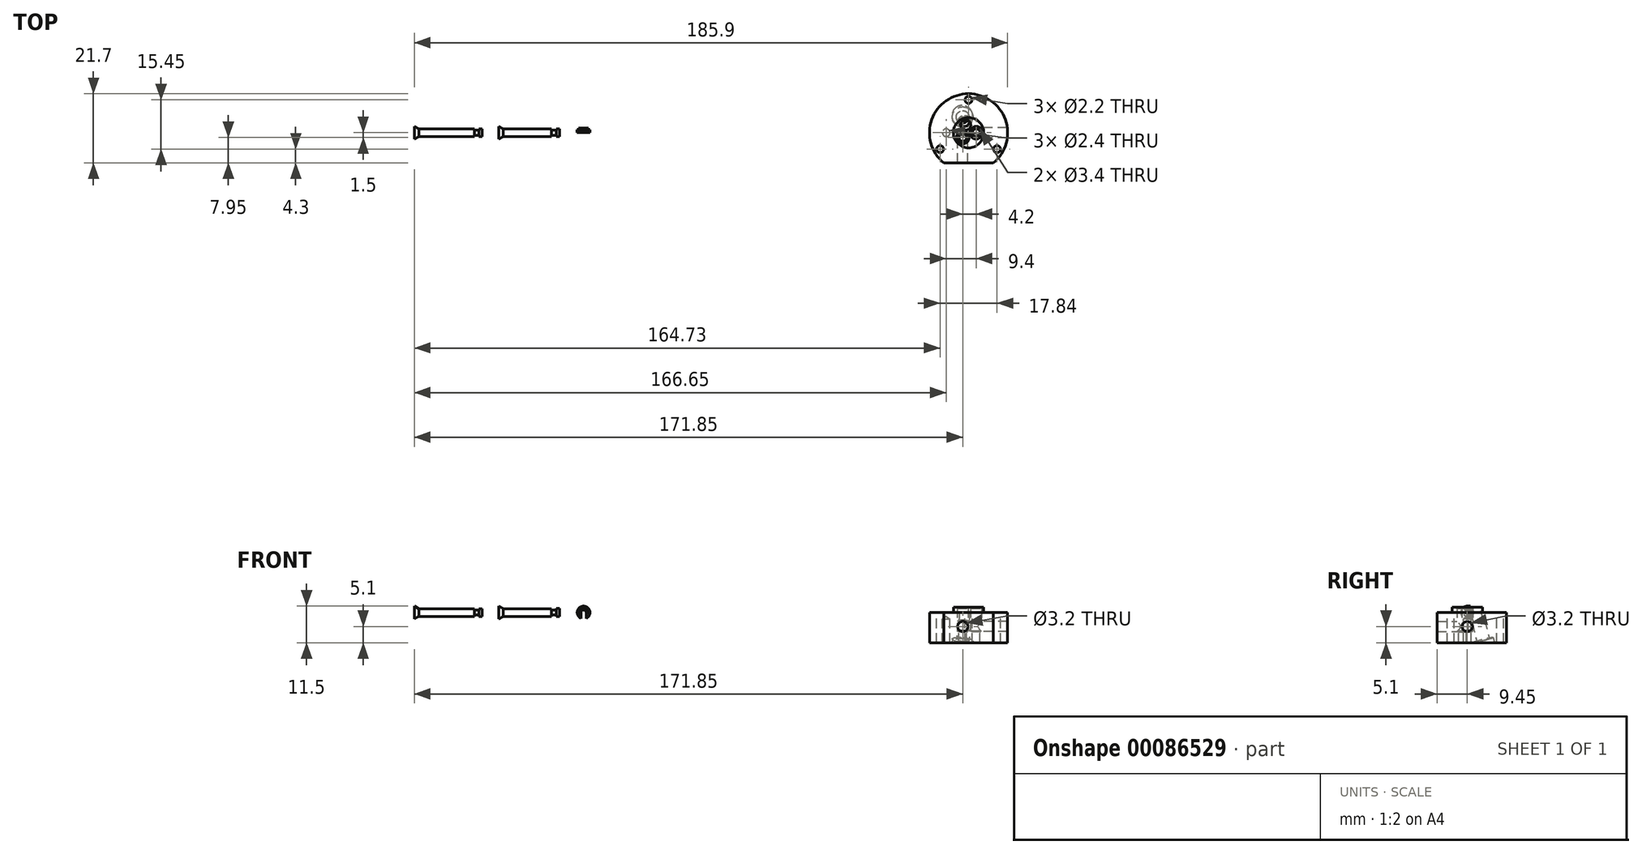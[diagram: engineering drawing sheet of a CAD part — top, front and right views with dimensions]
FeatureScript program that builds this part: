
annotation { "Feature Type Name" : "Feature", "Feature Type Description" : "" }
export const myFeature = defineFeature(function(context is Context, id is Id, definition is map)
    precondition{}
    {
        {
            var Q0;
            Q0=qCreatedBy(makeId("Top.planeOp"),FACE);
            var sketch = newSketch(context, id + "F0", { "sketchPlane" : qUnion([Q0])});
            skLineSegment(sketch, "E0", {"start": v(-7.8, -9.45) * mm, "end": v(7.8, -9.45) * mm});
            skPoint(sketch, "E1", {"position": v(0, 12.25) * mm});
            skArc(sketch, "E2", {"start": v(7.8, -9.45) * mm, "mid": v(0, 12.25) * mm, "end": v(-7.8, -9.45) * mm});
            skCircle(sketch, "E3", {"center": v(0, 0) * mm, "radius": 4.75 * mm});
            skCircle(sketch, "E4", {"center": v(0, 0) * mm, "radius": 10.3 * mm, "construction": true});
            skCircle(sketch, "E5", {"center": v(0, 10.3) * mm, "radius": 1.1 * mm});
            skCircle(sketch, "E6.1.0", {"center": v(-8.92, -5.15) * mm, "radius": 1.1 * mm});
            skCircle(sketch, "E6.2.0", {"center": v(8.92, -5.15) * mm, "radius": 1.1 * mm});
            skPoint(sketch, "E7", {"position": v(2.4, 0) * mm});
            skPoint(sketch, "E8", {"position": v(-1.8, -1.5) * mm});
            skSolve(sketch);
        }
        {
            var Q0;
            Q0=makeQuery(id+"F0.imprint","IMPRINT",FACE,{"disambiguationData":[TD([[makeQuery(id+"F0.imprint","IMPRINT",EDGE,{"derivedFrom":sQuery(id+"F0.wireOp",EDGE,"E0")}),1.0]])]});
            var Q1;
            Q1=makeQuery(id+"F0.imprint","IMPRINT",FACE,{"disambiguationData":[TD([[makeQuery(id+"F0.imprint","IMPRINT",EDGE,{"derivedFrom":sQuery(id+"F0.wireOp",EDGE,"E3")}),1.0]])]});
            extrude(context, id + "F1", {"entities" : qUnion([Q0, Q1]), "oppositeDirection" : true, "depth" : 9.5 * mm});
        }
        {
            var Q0;
            Q0=makeQuery(id+"F0.imprint","IMPRINT",FACE,{"disambiguationData":[TD([[makeQuery(id+"F0.imprint","IMPRINT",EDGE,{"derivedFrom":sQuery(id+"F0.wireOp",EDGE,"E3")}),1.0]])]});
            extrude(context, id + "F2", {"entities" : qUnion([Q0]), "operationType" : NewBodyOperationType.ADD, "depth" : 1.6 * mm});
        }
        {
            var Q0;
            Q0=makeQuery(id+"F2.opExtrude","CAP_FACE",FACE,{"disambiguationData":[OSD([sQuery(id+"F0.wireOp",EDGE,"E3"),sQuery(id+"F0.wireOp",EDGE,"RqqYGp9O-cIjH-IyXc-yckS-H4xSrRzo904b"),sQuery(id+"F0.wireOp",EDGE,"ZuBGWJ4k-Wu2v-yg4J-xYeN-5ZjtPgcVGRH9")])],"isStart":false});
            var sketch = newSketch(context, id + "F3", { "sketchPlane" : qUnion([Q0])});
            skPoint(sketch, "E9", {"position": v(-0.9, 2.4) * mm});
            skLineSegment(sketch, "E10", {"start": v(-0.9, 2.4) * mm, "end": v(-6.68, 0.23) * mm, "construction": true});
            skLineSegment(sketch, "E11.0", {"start": v(-0.34, 0.9) * mm, "end": v(-6.11, -1.26) * mm, "construction": true});
            skSolve(sketch);
        }
        {
            var Q0;
            Q0=qCreatedBy(makeId("Right.planeOp"),FACE);
            var Q1;
            Q1=sQuery(id+"F3.wireOp",EDGE,"E11.0");
            cPlane(context, id + "F4", {"entities" : qUnion([Q0, Q1]), "cplaneType" : CPlaneType.LINE_ANGLE, "offset" : 150 * mm, "angle" : 75 * degree, "width" : 150 * mm, "height" : 150 * mm});
        }
        {
            var Q0;
            Q0=qCreatedBy(id+"F4.planeOp",FACE);
            var sketch = newSketch(context, id + "F5", { "sketchPlane" : qUnion([Q0])});
            skCircle(sketch, "E12", {"center": v(-0.98, -2.72) * mm, "radius": 1.6 * mm});
            skSolve(sketch);
        }
        {
            var Q0;
            Q0=makeQuery(id+"F5.imprint","IMPRINT",FACE,{"disambiguationData":[TD([[makeQuery(id+"F5.imprint","IMPRINT",EDGE,{"derivedFrom":sQuery(id+"F5.wireOp",EDGE,"E12")}),1.0]])]});
            var Q1;
            Q1=qSketchRegion(id+"F3",true);
            extrude(context, id + "F6", {"entities" : qUnion([Q0, Q1]), "operationType" : NewBodyOperationType.REMOVE, "endBound" : BoundingType.THROUGH_ALL, "depth" : 25 * mm});
        }
        {
            var Q0;
            Q0=qCreatedBy(id+"F4.planeOp",FACE);
            cPlane(context, id + "F7", {"entities" : qUnion([Q0]), "cplaneType" : CPlaneType.OFFSET, "offset" : 15 * mm, "width" : 150 * mm, "height" : 150 * mm});
        }
        {
            var Q0;
            Q0=qCreatedBy(id+"F7.planeOp",FACE);
            var sketch = newSketch(context, id + "F8", { "sketchPlane" : qUnion([Q0])});
            skPoint(sketch, "E13.0", {"position": v(-0.98, -2.72) * mm});
            skCircle(sketch, "E14", {"center": v(-0.98, -2.72) * mm, "radius": 2 * mm});
            skSolve(sketch);
        }
        {
            var Q0;
            Q0=makeQuery(id+"F8.imprint","IMPRINT",FACE,{"disambiguationData":[TD([[makeQuery(id+"F8.imprint","IMPRINT",EDGE,{"derivedFrom":sQuery(id+"F8.wireOp",EDGE,"E14")}),1.0]])]});
            var Q1;
            Q1=sQuery(id+"F8.wireOp",EDGE,"E14");
            var Q2;
            Q2=makeQuery(id+"F1.opExtrude","CAP_FACE",FACE,{"disambiguationData":[OSD([sQuery(id+"F0.wireOp",EDGE,"E0"),sQuery(id+"F0.wireOp",EDGE,"E2"),sQuery(id+"F0.wireOp",EDGE,"E5"),sQuery(id+"F0.wireOp",EDGE,"E6.1.0"),sQuery(id+"F0.wireOp",EDGE,"E6.2.0"),sQuery(id+"F0.wireOp",EDGE,"RqqYGp9O-cIjH-IyXc-yckS-H4xSrRzo904b"),sQuery(id+"F0.wireOp",EDGE,"ZuBGWJ4k-Wu2v-yg4J-xYeN-5ZjtPgcVGRH9")])],"isStart":false});
            var Q3;
            Q3=makeQuery(id+"F1.opExtrude","SWEPT_BODY",BODY,{"disambiguationData":[OSD([sQuery(id+"F0.wireOp",EDGE,"E0"),sQuery(id+"F0.wireOp",EDGE,"E2"),sQuery(id+"F0.wireOp",EDGE,"E5"),sQuery(id+"F0.wireOp",EDGE,"E6.1.0"),sQuery(id+"F0.wireOp",EDGE,"E6.2.0"),sQuery(id+"F0.wireOp",EDGE,"RqqYGp9O-cIjH-IyXc-yckS-H4xSrRzo904b"),sQuery(id+"F0.wireOp",EDGE,"ZuBGWJ4k-Wu2v-yg4J-xYeN-5ZjtPgcVGRH9")])]});
            extrude(context, id + "F9", {"entities" : qUnion([Q0]), "operationType" : NewBodyOperationType.REMOVE, "surfaceEntities" : qUnion([Q1]), "oppositeDirection" : true, "endBoundEntityFace" : qUnion([Q2]), "endBoundEntityBody" : qUnion([Q3]), "depth" : 10 * mm});
        }
        {
            var Q0;
            Q0=qCreatedBy(id+"F7.planeOp",FACE);
            var sketch = newSketch(context, id + "F10", { "sketchPlane" : qUnion([Q0])});
            skCircle(sketch, "E15", {"center": v(-0.98, -2.72) * mm, "radius": 3.25 * mm});
            skSolve(sketch);
        }
        {
            var Q0;
            Q0=makeQuery(id+"F10.imprint","IMPRINT",FACE,{"disambiguationData":[TD([[makeQuery(id+"F10.imprint","IMPRINT",EDGE,{"derivedFrom":sQuery(id+"F10.wireOp",EDGE,"E15")}),1.0]])]});
            var Q1;
            Q1=sQuery(id+"F10.wireOp",EDGE,"E15");
            var Q2;
            Q2=makeQuery(id+"F1.opExtrude","CAP_FACE",FACE,{"disambiguationData":[OSD([sQuery(id+"F0.wireOp",EDGE,"E0"),sQuery(id+"F0.wireOp",EDGE,"E2"),sQuery(id+"F0.wireOp",EDGE,"E5"),sQuery(id+"F0.wireOp",EDGE,"E6.1.0"),sQuery(id+"F0.wireOp",EDGE,"E6.2.0"),sQuery(id+"F0.wireOp",EDGE,"RqqYGp9O-cIjH-IyXc-yckS-H4xSrRzo904b"),sQuery(id+"F0.wireOp",EDGE,"ZuBGWJ4k-Wu2v-yg4J-xYeN-5ZjtPgcVGRH9")])],"isStart":false});
            extrude(context, id + "F11", {"entities" : qUnion([Q0]), "operationType" : NewBodyOperationType.REMOVE, "surfaceEntities" : qUnion([Q1]), "oppositeDirection" : true, "endBoundEntityFace" : qUnion([Q2]), "depth" : 4 * mm});
        }
        {
            var Q0;
            Q0=makeQuery(id+"F3.imprint","IMPRINT",FACE,{"disambiguationData":[TD([[makeQuery(id+"F3.imprint","IMPRINT",EDGE,{"derivedFrom":makeQuery(id+"F2.opExtrude","CAP_EDGE",EDGE,{"disambiguationData":[OSD([sQuery(id+"F0.wireOp",EDGE,"E3")])],"isStart":false})}),1.0]])]});
            var sketch = newSketch(context, id + "F12", { "sketchPlane" : qUnion([Q0])});
            skLineSegment(sketch, "E16.0", {"start": v(-7.8, -9.45) * mm, "end": v(7.8, -9.45) * mm});
            skPoint(sketch, "E16.1", {"position": v(0, 12.25) * mm});
            skArc(sketch, "E16.2", {"start": v(7.8, -9.45) * mm, "mid": v(0, 12.25) * mm, "end": v(-7.8, -9.45) * mm});
            skCircle(sketch, "E16.3", {"center": v(0, 0) * mm, "radius": 4.75 * mm});
            skCircle(sketch, "E16.4", {"center": v(0, 0) * mm, "radius": 10.3 * mm});
            skCircle(sketch, "E16.5", {"center": v(0, 10.3) * mm, "radius": 1.1 * mm});
            skCircle(sketch, "E16.6", {"center": v(-8.92, -5.15) * mm, "radius": 1.1 * mm});
            skCircle(sketch, "E16.7", {"center": v(8.92, -5.15) * mm, "radius": 1.1 * mm});
            skPoint(sketch, "E16.8", {"position": v(0, 0) * mm});
            skPoint(sketch, "E16.9", {"position": v(2.4, 0) * mm});
            skPoint(sketch, "E16.10", {"position": v(-1.8, -1.5) * mm});
            skSolve(sketch);
        }
        {
            var Q0;
            Q0=sQuery(id+"F12.wireOp",VERTEX,"E16.10");
            var Q1;
            Q1=sQuery(id+"F12.wireOp",VERTEX,"E16.9");
            var Q2;
            Q2=makeQuery(id+"F1.opExtrude","SWEPT_BODY",BODY,{"disambiguationData":[OSD([sQuery(id+"F0.wireOp",EDGE,"E0"),sQuery(id+"F0.wireOp",EDGE,"E2"),sQuery(id+"F0.wireOp",EDGE,"E5"),sQuery(id+"F0.wireOp",EDGE,"E6.1.0"),sQuery(id+"F0.wireOp",EDGE,"E6.2.0")])]});
            hole(context, id + "F13", {"style" : HoleStyle.C_SINK, "endStyle" : HoleEndStyle.BLIND, "holeDiameter" : 3.4 * mm, "cSinkDiameter" : 4 * mm, "cSinkAngle" : 90 * degree, "holeDepth" : 7.4 * mm, "startFromSketch" : true, "locations" : qUnion([Q0, Q1]), "scope" : qUnion([Q2])});
        }
        {
            var Q0;
            Q0=makeQuery(id+"F1.opExtrude","CAP_FACE",FACE,{"disambiguationData":[OSD([sQuery(id+"F0.wireOp",EDGE,"E0"),sQuery(id+"F0.wireOp",EDGE,"E2"),sQuery(id+"F0.wireOp",EDGE,"E5"),sQuery(id+"F0.wireOp",EDGE,"E6.1.0"),sQuery(id+"F0.wireOp",EDGE,"E6.2.0")])],"isStart":false});
            var sketch = newSketch(context, id + "F14", { "sketchPlane" : qUnion([Q0])});
            skPoint(sketch, "E17.0", {"position": v(2.4, 0) * mm});
            skPoint(sketch, "E18.0", {"position": v(-1.8, 1.5) * mm});
            skSolve(sketch);
        }
        {
            var Q0;
            Q0=sQuery(id+"F14.wireOp",VERTEX,"E17.0");
            var Q1;
            Q1=sQuery(id+"F14.wireOp",VERTEX,"E18.0");
            var Q2;
            Q2=makeQuery(id+"F1.opExtrude","SWEPT_BODY",BODY,{"disambiguationData":[OSD([sQuery(id+"F0.wireOp",EDGE,"E0"),sQuery(id+"F0.wireOp",EDGE,"E2"),sQuery(id+"F0.wireOp",EDGE,"E5"),sQuery(id+"F0.wireOp",EDGE,"E6.1.0"),sQuery(id+"F0.wireOp",EDGE,"E6.2.0")])]});
            hole(context, id + "F15", {"style" : HoleStyle.SIMPLE, "endStyle" : HoleEndStyle.THROUGH, "holeDiameter" : 2.4 * mm, "startFromSketch" : true, "locations" : qUnion([Q0, Q1]), "scope" : qUnion([Q2]), "isTappedThrough" : true});
        }
        {
            var Q0;
            Q0=makeQuery(id+"F1.opExtrude","SWEPT_FACE",FACE,{"disambiguationData":[OSD([sQuery(id+"F0.wireOp",EDGE,"E0")])]});
            var sketch = newSketch(context, id + "F16", { "sketchPlane" : qUnion([Q0])});
            skLineSegment(sketch, "E19.0", {"start": v(-3.5, 1.3) * mm, "end": v(-0.1, 1.3) * mm});
            skLineSegment(sketch, "E20", {"start": v(-1.8, 1.3) * mm, "end": v(-1.8, -9.5) * mm, "construction": true});
            skLineSegment(sketch, "E21", {"start": v(-1.8, 1.3) * mm, "end": v(-3.5, 1.3) * mm});
            skLineSegment(sketch, "E22", {"start": v(-1.8, 1.3) * mm, "end": v(-0.1, 1.3) * mm});
            skPoint(sketch, "E23", {"position": v(-1.8, -4.4) * mm});
            skSolve(sketch);
        }
        {
            var Q0;
            Q0=sQuery(id+"F16.wireOp",VERTEX,"E23");
            var Q1;
            Q1=makeQuery(id+"F1.opExtrude","SWEPT_BODY",BODY,{"disambiguationData":[OSD([sQuery(id+"F0.wireOp",EDGE,"E0"),sQuery(id+"F0.wireOp",EDGE,"E2"),sQuery(id+"F0.wireOp",EDGE,"E5"),sQuery(id+"F0.wireOp",EDGE,"E6.1.0"),sQuery(id+"F0.wireOp",EDGE,"E6.2.0")])]});
            hole(context, id + "F17", {"style" : HoleStyle.SIMPLE, "endStyle" : HoleEndStyle.BLIND, "holeDiameter" : 3.2 * mm, "holeDepth" : 7.5 * mm, "startFromSketch" : true, "locations" : qUnion([Q0]), "scope" : qUnion([Q1])});
        }
        {
            var Q0;
            Q0=makeQuery(id+"F1.opExtrude","CAP_FACE",FACE,{"disambiguationData":[OSD([sQuery(id+"F0.wireOp",EDGE,"E0"),sQuery(id+"F0.wireOp",EDGE,"E2"),sQuery(id+"F0.wireOp",EDGE,"E5"),sQuery(id+"F0.wireOp",EDGE,"E6.1.0"),sQuery(id+"F0.wireOp",EDGE,"E6.2.0")])],"isStart":false});
            var sketch = newSketch(context, id + "F18", { "sketchPlane" : qUnion([Q0])});
            skPoint(sketch, "E24", {"position": v(-7, 0) * mm});
            skSolve(sketch);
        }
        {
            var Q0;
            Q0=sQuery(id+"F18.wireOp",VERTEX,"E24");
            var Q1;
            Q1=makeQuery(id+"F1.opExtrude","SWEPT_BODY",BODY,{"disambiguationData":[OSD([sQuery(id+"F0.wireOp",EDGE,"E0"),sQuery(id+"F0.wireOp",EDGE,"E2"),sQuery(id+"F0.wireOp",EDGE,"E5"),sQuery(id+"F0.wireOp",EDGE,"E6.1.0"),sQuery(id+"F0.wireOp",EDGE,"E6.2.0")])]});
            hole(context, id + "F19", {"style" : HoleStyle.SIMPLE, "endStyle" : HoleEndStyle.BLIND, "standardTappedOrClearance" : lookupTablePath({ "standard" : "ISO", "engagement" : "75%", "pitch" : "0.6 mm", "size" : "M3", "type" : "Tapped" }), "standardBlindInLast" : lookupTablePath({ "standard" : "ISO", "engagement" : "75%", "pitch" : "0.6 mm", "size" : "M3", "type" : "Tapped" }), "holeDiameter" : 2.4 * mm, "holeDepth" : 7.5 * mm, "startFromSketch" : true, "locations" : qUnion([Q0]), "scope" : qUnion([Q1])});
        }
        {
            var Q0;
            Q0=qCreatedBy(makeId("Right.planeOp"),FACE);
            cPlane(context, id + "F20", {"entities" : qUnion([Q0]), "cplaneType" : CPlaneType.OFFSET, "offset" : 12.25 * mm, "width" : 150 * mm, "height" : 150 * mm});
        }
        {
            var Q0;
            Q0=qCreatedBy(id+"F20.planeOp",FACE);
            var sketch = newSketch(context, id + "F21", { "sketchPlane" : qUnion([Q0])});
            skPoint(sketch, "E25", {"position": v(0, -4.4) * mm});
            skSolve(sketch);
        }
        {
            var Q0;
            Q0=sQuery(id+"F21.wireOp",VERTEX,"E25");
            var Q1;
            Q1=makeQuery(id+"F1.opExtrude","SWEPT_BODY",BODY,{"disambiguationData":[OSD([sQuery(id+"F0.wireOp",EDGE,"E0"),sQuery(id+"F0.wireOp",EDGE,"E2"),sQuery(id+"F0.wireOp",EDGE,"E5"),sQuery(id+"F0.wireOp",EDGE,"E6.1.0"),sQuery(id+"F0.wireOp",EDGE,"E6.2.0")])]});
            hole(context, id + "F22", {"style" : HoleStyle.SIMPLE, "endStyle" : HoleEndStyle.BLIND, "holeDiameter" : 3.2 * mm, "holeDepth" : 10 * mm, "startFromSketch" : true, "locations" : qUnion([Q0]), "scope" : qUnion([Q1])});
        }
        {
            var Q0;
            Q0=qCreatedBy(makeId("Front.planeOp"),FACE);
            var sketch = newSketch(context, id + "F23", { "sketchPlane" : qUnion([Q0])});
            skLineSegment(sketch, "E26", {"start": v(-77.35, 0) * mm, "end": v(-98.65, 0) * mm});
            skLineSegment(sketch, "E27", {"start": v(-98.65, 0) * mm, "end": v(-98.65, 2) * mm});
            skLineSegment(sketch, "E28", {"start": v(-77.35, 0) * mm, "end": v(-77.35, 1.2) * mm});
            skLineSegment(sketch, "E29", {"start": v(-98.65, 2) * mm, "end": v(-97.26, 1.2) * mm});
            skLineSegment(sketch, "E30", {"start": v(-77.35, 1.2) * mm, "end": v(-78.35, 1.2) * mm});
            skLineSegment(sketch, "E31", {"start": v(-78.35, 1.2) * mm, "end": v(-78.35, 0.8) * mm});
            skLineSegment(sketch, "E32", {"start": v(-78.35, 0.8) * mm, "end": v(-79.85, 0.8) * mm});
            skLineSegment(sketch, "E33", {"start": v(-79.85, 0.8) * mm, "end": v(-79.85, 1.2) * mm});
            skLineSegment(sketch, "E34", {"start": v(-79.85, 1.2) * mm, "end": v(-97.26, 1.2) * mm});
            skSolve(sketch);
        }
        {
            var Q0;
            Q0=makeQuery(id+"F23.imprint","IMPRINT",FACE,{"disambiguationData":[TD([[makeQuery(id+"F23.imprint","IMPRINT",EDGE,{"derivedFrom":sQuery(id+"F23.wireOp",EDGE,"E26")}),-1.0]])]});
            var Q1;
            Q1=sQuery(id+"F23.wireOp",EDGE,"E26");
            revolve(context, id + "F24", {"entities" : qUnion([Q0]), "axis" : qUnion([Q1]), "revolveType" : RevolveType.FULL});
        }
        {
            var Q0;
            Q0=qCreatedBy(makeId("Front.planeOp"),FACE);
            var sketch = newSketch(context, id + "F25", { "sketchPlane" : qUnion([Q0])});
            skArc(sketch, "E35", {"start": v(-44.82, -1.83) * mm, "mid": v(-45.62, 2) * mm, "end": v(-46.42, -1.83) * mm});
            skArc(sketch, "E36", {"start": v(-44.82, -0.9) * mm, "mid": v(-45.62, 1.2) * mm, "end": v(-46.42, -0.9) * mm});
            skArc(sketch, "E37", {"start": v(-44.82, -1.27) * mm, "mid": v(-45.62, 1.5) * mm, "end": v(-46.42, -1.27) * mm});
            skArc(sketch, "E38", {"start": v(-44.82, 0) * mm, "mid": v(-45.62, 0.8) * mm, "end": v(-46.42, 0) * mm});
            skLineSegment(sketch, "E39", {"start": v(-46.42, 0) * mm, "end": v(-46.42, -1.83) * mm});
            skLineSegment(sketch, "E40", {"start": v(-44.82, 0) * mm, "end": v(-44.82, -1.83) * mm});
            skSolve(sketch);
        }
        {
            var Q0;
            {var subQ0=sQuery(id+"F25.wireOp",EDGE,"E35");Q0=makeQuery(id+"F25.imprint","IMPRINT",FACE,{"disambiguationData":[TD([[makeQuery(id+"F25.imprint","IMPRINT",EDGE,{"derivedFrom":subQ0}),1.0]])]});}
            var Q1;
            {var subQ0=sQuery(id+"F25.wireOp",EDGE,"E36");Q1=makeQuery(id+"F25.imprint","IMPRINT",FACE,{"disambiguationData":[TD([[makeQuery(id+"F25.imprint","IMPRINT",EDGE,{"derivedFrom":subQ0}),1.0]])]});}
            var Q2;
            {var subQ0=sQuery(id+"F25.wireOp",EDGE,"E36");Q2=makeQuery(id+"F25.imprint","IMPRINT",FACE,{"disambiguationData":[TD([[makeQuery(id+"F25.imprint","IMPRINT",EDGE,{"derivedFrom":subQ0}),-1.0]])]});}
            extrude(context, id + "F26", {"entities" : qUnion([Q0, Q1, Q2]), "oppositeDirection" : true, "depth" : 1 * mm});
        }
        {
            var Q0;
            {var subQ0=sQuery(id+"F25.wireOp",EDGE,"E36");Q0=makeQuery(id+"F25.imprint","IMPRINT",FACE,{"disambiguationData":[TD([[makeQuery(id+"F25.imprint","IMPRINT",EDGE,{"derivedFrom":subQ0}),1.0]])]});}
            var Q1;
            {var subQ0=sQuery(id+"F25.wireOp",EDGE,"E36");Q1=makeQuery(id+"F25.imprint","IMPRINT",FACE,{"disambiguationData":[TD([[makeQuery(id+"F25.imprint","IMPRINT",EDGE,{"derivedFrom":subQ0}),-1.0]])]});}
            extrude(context, id + "F27", {"entities" : qUnion([Q0, Q1]), "operationType" : NewBodyOperationType.ADD, "oppositeDirection" : true, "depth" : 1.5 * mm});
        }
        {
            var Q0;
            {var subQ0=sQuery(id+"F25.wireOp",EDGE,"E36");Q0=makeQuery(id+"F25.imprint","IMPRINT",FACE,{"disambiguationData":[TD([[makeQuery(id+"F25.imprint","IMPRINT",EDGE,{"derivedFrom":subQ0}),1.0]])]});}
            extrude(context, id + "F28", {"entities" : qUnion([Q0]), "operationType" : NewBodyOperationType.REMOVE, "oppositeDirection" : true, "depth" : .5 * mm});
        }
        {
            var Q0;
            Q0=qCreatedBy(makeId("Front.planeOp"),FACE);
            var sketch = newSketch(context, id + "F29", { "sketchPlane" : qUnion([Q0])});
            skLineSegment(sketch, "E41", {"start": v(-72.15, 0) * mm, "end": v(-52.38, 0) * mm, "construction": true});
            skLineSegment(sketch, "E42", {"start": v(-72.15, 0) * mm, "end": v(-72.15, 2) * mm});
            skLineSegment(sketch, "E43", {"start": v(-72.15, 2) * mm, "end": v(-70.77, 1.2) * mm});
            skLineSegment(sketch, "E44", {"start": v(-70.77, 1.2) * mm, "end": v(-55.65, 1.2) * mm});
            skLineSegment(sketch, "E45", {"start": v(-55.65, 1.2) * mm, "end": v(-55.65, 0.8) * mm});
            skLineSegment(sketch, "E46", {"start": v(-55.65, 0.8) * mm, "end": v(-54.15, 0.8) * mm});
            skLineSegment(sketch, "E47", {"start": v(-54.15, 0.8) * mm, "end": v(-54.15, 1.26) * mm});
            skLineSegment(sketch, "E48", {"start": v(-54.15, 1.26) * mm, "end": v(-53.15, 1.26) * mm});
            skLineSegment(sketch, "E49", {"start": v(-53.15, 1.26) * mm, "end": v(-53.15, 0) * mm});
            skLineSegment(sketch, "E50", {"start": v(-53.15, 0) * mm, "end": v(-72.15, 0) * mm});
            skSolve(sketch);
        }
        {
            var Q0;
            Q0=makeQuery(id+"F29.imprint","IMPRINT",FACE,{"disambiguationData":[TD([[makeQuery(id+"F29.imprint","IMPRINT",EDGE,{"derivedFrom":sQuery(id+"F29.wireOp",EDGE,"E42")}),-1.0]])]});
            var Q1;
            Q1=sQuery(id+"F29.wireOp",EDGE,"E41");
            revolve(context, id + "F30", {"entities" : qUnion([Q0]), "axis" : qUnion([Q1]), "revolveType" : RevolveType.FULL});
        }
        {
            var Q0;
            Q0=makeQuery(id+"F1.opExtrude","SWEPT_BODY",BODY,{"disambiguationData":[OSD([sQuery(id+"F0.wireOp",EDGE,"E0"),sQuery(id+"F0.wireOp",EDGE,"E2"),sQuery(id+"F0.wireOp",EDGE,"E5"),sQuery(id+"F0.wireOp",EDGE,"E6.1.0"),sQuery(id+"F0.wireOp",EDGE,"E6.2.0")])]});
            var Q1;
            Q1=qCreatedBy(makeId("Right.planeOp"),FACE);
            transform(context, id + "F31", {"entities" : qUnion([Q0]), "transformType" : TransformType.TRANSLATION_DISTANCE, "transformDirection" : qUnion([Q1]), "distance" : 75 * mm, "makeCopy" : false});
        }
    });
